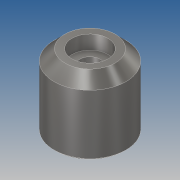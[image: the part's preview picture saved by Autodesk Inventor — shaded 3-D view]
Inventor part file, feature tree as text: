
AUTODESK INVENTOR PART (.ipt)
format: ipt  version: 2018.2 (Build 222227000, 227)  size: 120,320 bytes
history: native  units: mm
features: sketch x3, hole x2, chamfer x2, extrude x1
ambient origin geometry x8: Origin, YZ Plane, XZ Plane, XY Plane, X Axis, Y Axis, Z Axis, Center Point
bodies: Volumenkörper1 (feature_tree)
feature tree (8):
  extrude  "Grundkörper"  Depth=20.0mm TaperAngle=0.0deg
  hole  "12H7_Passbohrung"  [1 undecoded]
  hole  "DIN7984_M5_Bohrung"  [1 undecoded]
  chamfer  "Fase_Deckel"  [1 undecoded]
  chamfer  "Fase_Allgemein"  [1 undecoded]
  sketch  "Skizze2"  dims[d0=20.0mm d1=20.0mm d2=0.0mm]
  sketch  "Skizze3"  dims[d3=12.0mm d4=6.0mm d5=4.0mm d6=2.0mm d7=90.0deg d8=10.0mm d9=0.0mm]
  sketch  "Skizze4"  dims[d10=5.5mm d11=6.0mm d12=10.0mm d13=3.9mm d14=90.0deg d15=10.0mm d16=20.594885mm d17=3.0mm d18=2.0mm d19=45.0deg d20=0.5mm d21=2.0mm d22=45.0deg]
note: 4 required parameter values undecoded (feature->parameter linkage not recoverable at this tier; creation-order binding heuristic only, values carry confidence <= 0.55)
